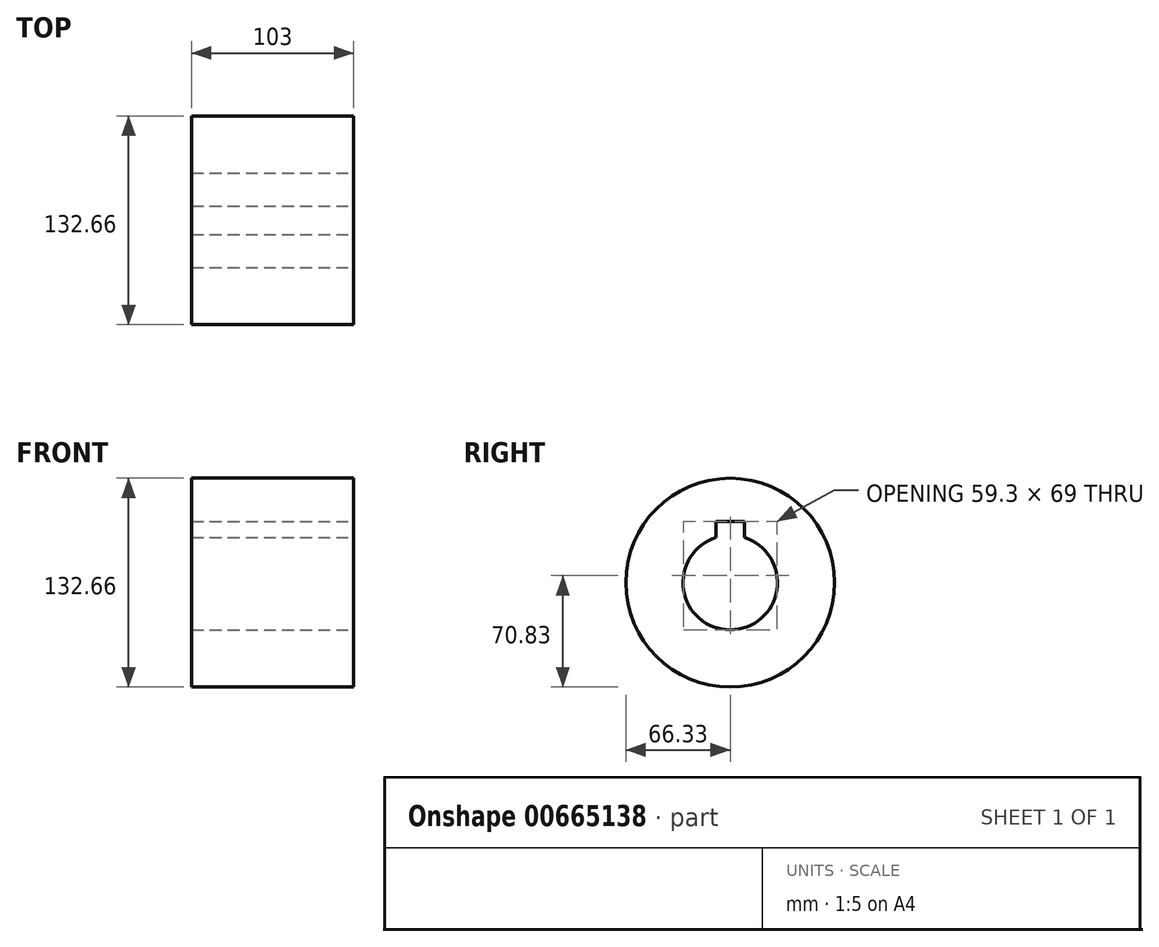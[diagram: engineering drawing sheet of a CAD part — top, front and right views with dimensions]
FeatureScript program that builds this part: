
annotation { "Feature Type Name" : "Feature", "Feature Type Description" : "" }
export const myFeature = defineFeature(function(context is Context, id is Id, definition is map)
    precondition{}
    {
        {
            var Q0;
            Q0=qCreatedBy(makeId("Right.planeOp"),FACE);
            var sketch = newSketch(context, id + "F0", { "sketchPlane" : qUnion([Q0])});
            skCircle(sketch, "E0", {"center": v(0, 0) * mm, "radius": 66.33 * mm});
            skSolve(sketch);
        }
        {
            var Q0;
            Q0 = qSketchRegion(id + "F0", true);
            extrude(context, id + "F1", {"entities" : qUnion([Q0]), "depth" : 103 * mm, "offsetDistance" : 25 * mm});
        }
        {
            var Q0;
            Q0=makeQuery(id+"F1.opExtrude","CAP_FACE",FACE,{"disambiguationData":[OSD([sQuery(id+"F0.wireOp",EDGE,"E0")])],"isStart":false});
            var sketch = newSketch(context, id + "F2", { "sketchPlane" : qUnion([Q0])});
            skArc(sketch, "E1", {"start": v(-9, 28.62) * mm, "mid": v(0, -30) * mm, "end": v(9, 28.62) * mm});
            skLineSegment(sketch, "E2", {"start": v(9, 39) * mm, "end": v(-9, 39) * mm});
            skLineSegment(sketch, "E3", {"start": v(-9, 39) * mm, "end": v(-9, 28.62) * mm});
            skLineSegment(sketch, "E4", {"start": v(9, 39) * mm, "end": v(9, 28.62) * mm});
            skSolve(sketch);
        }
        {
            var Q0;
            Q0 = qSketchRegion(id + "F2", true);
            extrude(context, id + "F3", {"entities" : qUnion([Q0]), "operationType" : NewBodyOperationType.REMOVE, "endBound" : BoundingType.THROUGH_ALL, "oppositeDirection" : true, "depth" : 25 * mm, "offsetDistance" : 25 * mm});
        }
    });
